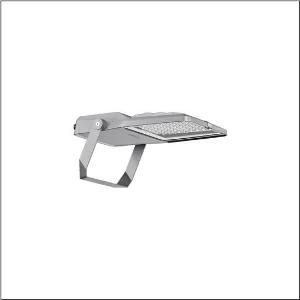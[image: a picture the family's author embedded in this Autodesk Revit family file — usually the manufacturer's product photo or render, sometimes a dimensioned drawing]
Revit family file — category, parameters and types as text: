
# Revit family: floodlight_fl_21_iq_mini___rs12_5xa7771d2b1a_498a
name_source: partatom
category: Lighting Fixtures
units: mm (PartAtom-declared; Revit-internal decimal feet)

## family parameters
Cut with Voids When Loaded = No
Host = Face
Light Source = No
Part Type = Normal
Room Calculation Point = No
Round Connector Dimension = Use Diameter
Shared = No

## types (1)
- --- (1 x LED, 18020 lm, 143 W, 3000K)
    Apparent Load = 143 VA
    CIE Flux Codes = 79 92 99 100 100
    Color Rendering = 70
    Color Temperature = 3000K
    Default Elevation = 1800 mm
    Description = Floodlight FL 21 iQ mini, floodlight, primary light control with lens, of PMMA, primary optical cover: protective disc, of toughened safety glass, transparent, light distribution: RS12, light emission: direct distribution, installation type: surface-mounted, LED, High Power LED, rated luminous flux: 18.020lm, luminous efficacy: 126lm/W, light colour: 730, colour temperature: 3000K, control: Auto-Match, Temp-Guard, Lumen-Switch, Night-Set, Smart-Wire, Light-Fading, Desk-Remote (wireless, voltage-free reading and setting of iQ features in the workshop via application-optimized NFC function/RFID function), optimised constant luminous flux control (CLO 2.0), with terminal, 6-pole, mains connection: 220..240V, AC, 50/60Hz, start of lifetime: 143W, end of service life: 152W, reduction: 61W, luminaire housing, of diecast aluminium, powder-coated, Siteco® metallic grey (DB 702S), corrosivity category C5 mid according to DIN EN ISO 12944, sealing non-destructively replaceable, mounting bracket, of steel, galvanised, powder-coated, Siteco® metallic grey (DB 702S), protection rating (complete): IP66, insulation class (complete): insulation class II (safety insulation), certification: CE, ENEC, VDE, protection symbol: D, impact resistance: IK08, permissible operating ambient temperature: -40..+40°C, permissible operating ambient temperature for outdoor applications: -40..+50°C, standard: DIN EN 12944, LABS conformity tested according to VDMA 24364:2018-05, packaging unit: 1 piece

Light Distribution: RS12
    Height = 70 mm
    Lamp = 1 x LED
    Lamp Light Flux = 18020 lm
    Lamp Power = 143 W
    Lamp count = 1
    Length = 485 mm
    Luminous efficacy = 126 lm/W
    Manufacturer = Siteco
    ModVariant = No
    Model = 5XA7771D2B1A
    Number of Poles = 1
    OnlyDefault = Yes
    Power Factor = 1
    Product Name = Floodlight FL 21 iQ mini | RS12
    Product group = floodlight | pylon annexe
    ProductGroupID = 6200
    Protection Class = Protection class II
    Protection Degree = IP 66
    RLX_Detail_Level = 1
    RLX_Emergency_Light_Flux = 0 lm
    RLX_Emergency_Type = 0
    RLX_Emergency_Type_DB = No
    RlxData = <blob elided: 90997 chars, md5=cf17693b>
    Socket = socket
    Standby Power = 0 W
    System Light Flux = 18020 lm
    System Power = 143 W
    Type Comments = factory setting: luminous flux: 100 % | dim-lin: 254 | 730 mA
    Type Image = l_1006845.jpg
    URL = http://relux.com
    VarID = @adj_099805
    Voltage = 0 V
    Weight = 0.00 kg
    Width = 337 mm

## geometry (parser evidence)
native form markers: Blend x4, Sweep x13
no freeform markers — native parametric forms only
